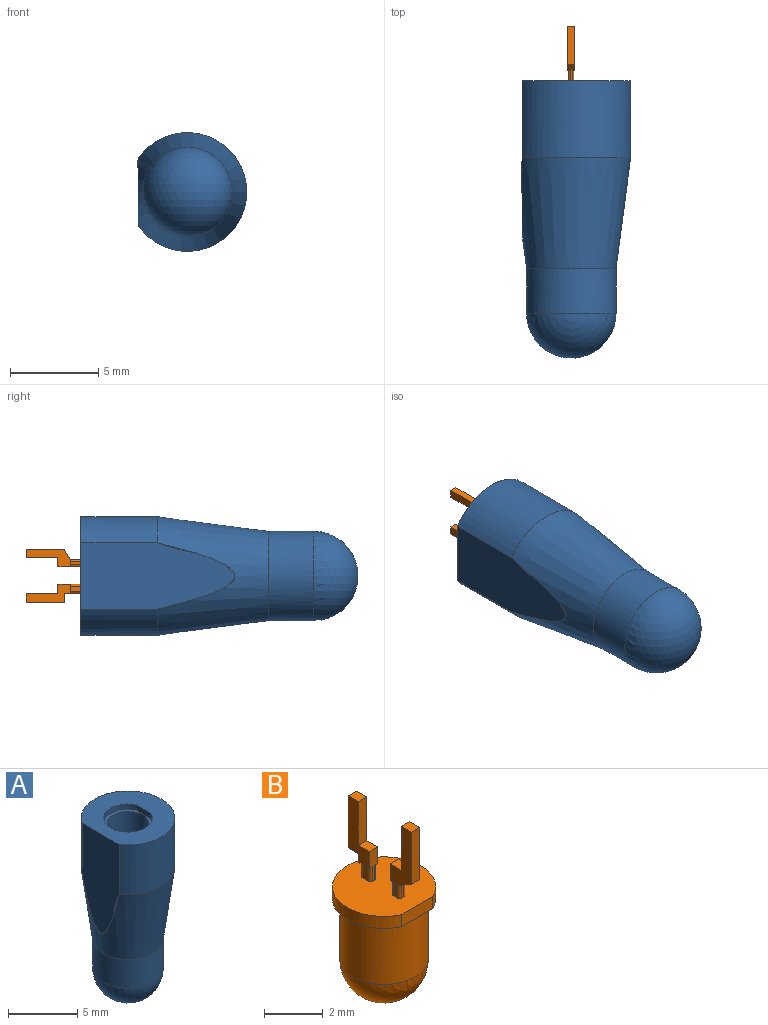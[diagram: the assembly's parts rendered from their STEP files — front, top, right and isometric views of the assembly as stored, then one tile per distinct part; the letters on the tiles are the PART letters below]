
ASSEMBLY  parts=2 mates=1
PART A: 11 faces, bbox 7.7x7.7x16.7 mm
  f0: sphere r=2.54mm, area 40.5mm2, adj f1
  f1: cylinder r=2.54mm len=5.08mm, axis (0,0,1), area 40.5mm2, adj f0,f2
  f2: cone r=2.54mm half-angle=7.5deg, axis (0,0,1), area 109.6mm2, adj f1,f3,f5
  f3: cylinder r=3.37mm len=6.74mm, axis (0,0,-1), area 75.1mm2, adj f2,f4,f5
  f4: plane 6.74x6.16mm, normal (0,0,1), area 24.7mm2, adj f3,f5,f8,f10
  f5: plane 9.67x4.7mm, normal (-1,0,0), area 27.2mm2, adj f2,f3,f4
  f6: sphere r=1.5mm, area 14.1mm2, adj f7
  f7: cylinder r=1.5mm len=3mm, axis (0,0,1), area 23.6mm2, adj f6,f9
  f8: cylinder r=1.75mm len=3.5mm, axis (0,0,1), area 4.5mm2, adj f4,f9,f10
  f9: plane 3.5x3.33mm, normal (0,0,1), area 2.4mm2, adj f7,f8,f10
  f10: plane 1.5x0.48mm, normal (-1,0,0), area 0.7mm2, adj f4,f8,f9
PART B: 40 faces, bbox 3.5x3.3x7.6 mm
  f0: sphere r=1.5mm, area 14.1mm2, adj f1
  f1: cylinder r=1.5mm len=3mm, axis (0,0,1), area 23.6mm2, adj f0,f12
  f2: cylinder r=1.75mm len=3.5mm, axis (0,0,1), area 4.7mm2, adj f11,f12,f13
  f3: plane 1.81x0.4mm, normal (0,-1,0), area 0.7mm2, adj f5,f6,f32,f39
  f4: plane 2.16x0.4mm, normal (0,1,0), area 0.9mm2, adj f5,f6,f33,f39
  f5: plane 2.51x1.02mm, normal (1,0,0), area 1.4mm2, adj f3,f4,f23,f27,f30,f32,f33,f39
  f6: plane 2.51x1.02mm, normal (-1,0,0), area 1.4mm2, adj f3,f4,f23,f27,f31,f32,f33,f39
  f7: plane 1.81x0.4mm, normal (0,1,0), area 0.7mm2, adj f9,f10,f37,f38
  f8: plane 2.16x0.4mm, normal (0,-1,0), area 0.9mm2, adj f9,f10,f35,f38
  f9: plane 2.51x1mm, normal (1,0,0), area 1.5mm2, adj f7,f8,f17,f34,f35,f37,f38
  f10: plane 2.51x1mm, normal (-1,0,0), area 1.5mm2, adj f7,f8,f17,f35,f36,f37,f38
  f11: plane 3.5x3.33mm, normal (0,0,1), area 9.2mm2, adj f2,f13,f14,f15,f16,f17,f18,f19
  f12: plane 3.5x3.33mm, normal (0,0,-1), area 2.4mm2, adj f1,f2,f13
  f13: plane 1.5x0.5mm, normal (0,-1,0), area 0.8mm2, adj f2,f11,f12
  f14: cylinder r=0.1mm len=0.6mm, axis (0,0,-1), area 0.1mm2, adj f11,f15,f21,f34
  f15: plane 0.6x0.2mm, normal (1,0,0), area 0.1mm2, adj f11,f14,f16,f34
  f16: cylinder r=0.1mm len=0.6mm, axis (0,0,-1), area 0.1mm2, adj f11,f15,f17,f34
  f17: plane 1.3x0.4mm, normal (0,1,0), area 0.3mm2, adj f9,f10,f11,f16,f18,f34,f36,f37
  f18: cylinder r=0.1mm len=0.6mm, axis (0,0,-1), area 0.1mm2, adj f11,f17,f19,f36
  f19: plane 0.6x0.2mm, normal (-1,0,0), area 0.1mm2, adj f11,f18,f20,f36
  f20: cylinder r=0.1mm len=0.6mm, axis (0,0,-1), area 0.1mm2, adj f11,f19,f21,f36
  f21: plane 0.6x0.1mm, normal (0,-1,0), area 0.1mm2, adj f11,f14,f20,f35
  f22: cylinder r=0.1mm len=0.6mm, axis (0,0,-1), area 0.1mm2, adj f11,f23,f29,f31
  f23: plane 1.3x0.4mm, normal (0,-1,0), area 0.3mm2, adj f5,f6,f11,f22,f24,f30,f31,f32
  f24: cylinder r=0.1mm len=0.6mm, axis (0,0,-1), area 0.1mm2, adj f11,f23,f25,f30
  f25: plane 0.6x0.3mm, normal (1,0,0), area 0.2mm2, adj f11,f24,f26,f30
  f26: cylinder r=0.1mm len=0.6mm, axis (0,0,-1), area 0.1mm2, adj f11,f25,f27,f30
  f27: plane 0.95x0.4mm, normal (0,1,0), area 0.2mm2, adj f5,f6,f11,f26,f28,f30,f31,f33
  f28: cylinder r=0.1mm len=0.6mm, axis (0,0,-1), area 0.1mm2, adj f11,f27,f29,f31
  f29: plane 0.6x0.3mm, normal (-1,0,0), area 0.2mm2, adj f11,f22,f28,f31
  f30: plane 0.5x0.15mm, normal (0,0,-1), area 0mm2, adj f5,f23,f24,f25,f26,f27
  f31: plane 0.5x0.15mm, normal (0,0,-1), area 0mm2, adj f6,f22,f23,f27,f28,f29
  f32: plane 0.54x0.4mm, normal (0,0,1), area 0.2mm2, adj f3,f5,f6,f23
  f33: plane 0.52x0.4mm, normal (0,0,-1), area 0.2mm2, adj f4,f5,f6,f27
  f34: plane 0.4x0.15mm, normal (0,0,-1), area 0mm2, adj f9,f14,f15,f16,f17,f35
  f35: plane 0.6x0.4mm, normal (0,-0.5,-0.86), area 0.3mm2, adj f8,f9,f10,f21,f34,f36
  f36: plane 0.4x0.15mm, normal (0,0,-1), area 0mm2, adj f10,f17,f18,f19,f20,f35
  f37: plane 0.52x0.4mm, normal (0,0,1), area 0.2mm2, adj f7,f9,f10,f17
  f38: plane 0.48x0.4mm, normal (0,0,1), area 0.2mm2, adj f7,f8,f9,f10
  f39: plane 0.48x0.4mm, normal (0,0,1), area 0.2mm2, adj f3,f4,f5,f6
PLACE A rot(axis=(-1,0,0),90deg) t=(-5.42,-5.45,-11.79)mm
PLACE B rot(axis=(-1,0,0),90deg) t=(-5.42,-2.27,-11.76)mm
MATE fastened B.f11 <-> A.f3  axis (0,1,0) through (-5.42,-1.08,-11.79)mm
